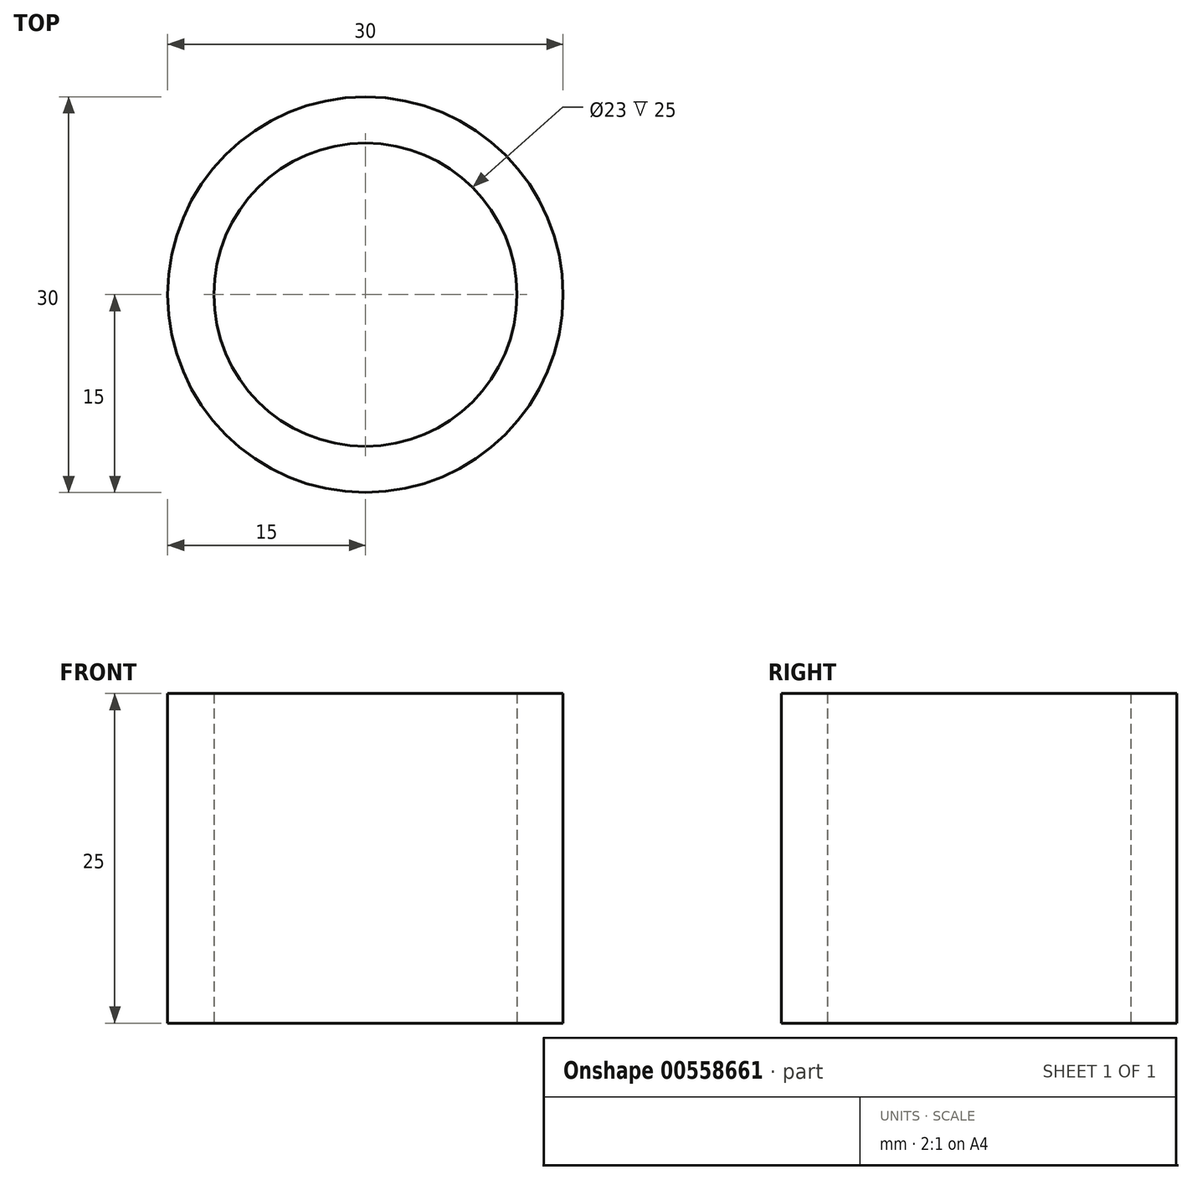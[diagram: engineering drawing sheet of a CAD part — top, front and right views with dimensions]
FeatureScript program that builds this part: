
annotation { "Feature Type Name" : "Feature", "Feature Type Description" : "" }
export const myFeature = defineFeature(function(context is Context, id is Id, definition is map)
    precondition{}
    {
        {
            var Q0;
            Q0=qCreatedBy(makeId("Top.planeOp"),FACE);
            var sketch = newSketch(context, id + "F0", { "sketchPlane" : qUnion([Q0])});
            skCircle(sketch, "E0", {"center": v(0, 0) * mm, "radius": 15 * mm});
            skCircle(sketch, "E1", {"center": v(0, 0) * mm, "radius": 11.5 * mm});
            skSolve(sketch);
        }
        {
            var Q0;
            Q0 = qSketchRegion(id + "F0", true);
            extrude(context, id + "F1", {"entities" : qUnion([Q0]), "depth" : 25 * mm, "offsetDistance" : 25 * mm});
        }
    });
